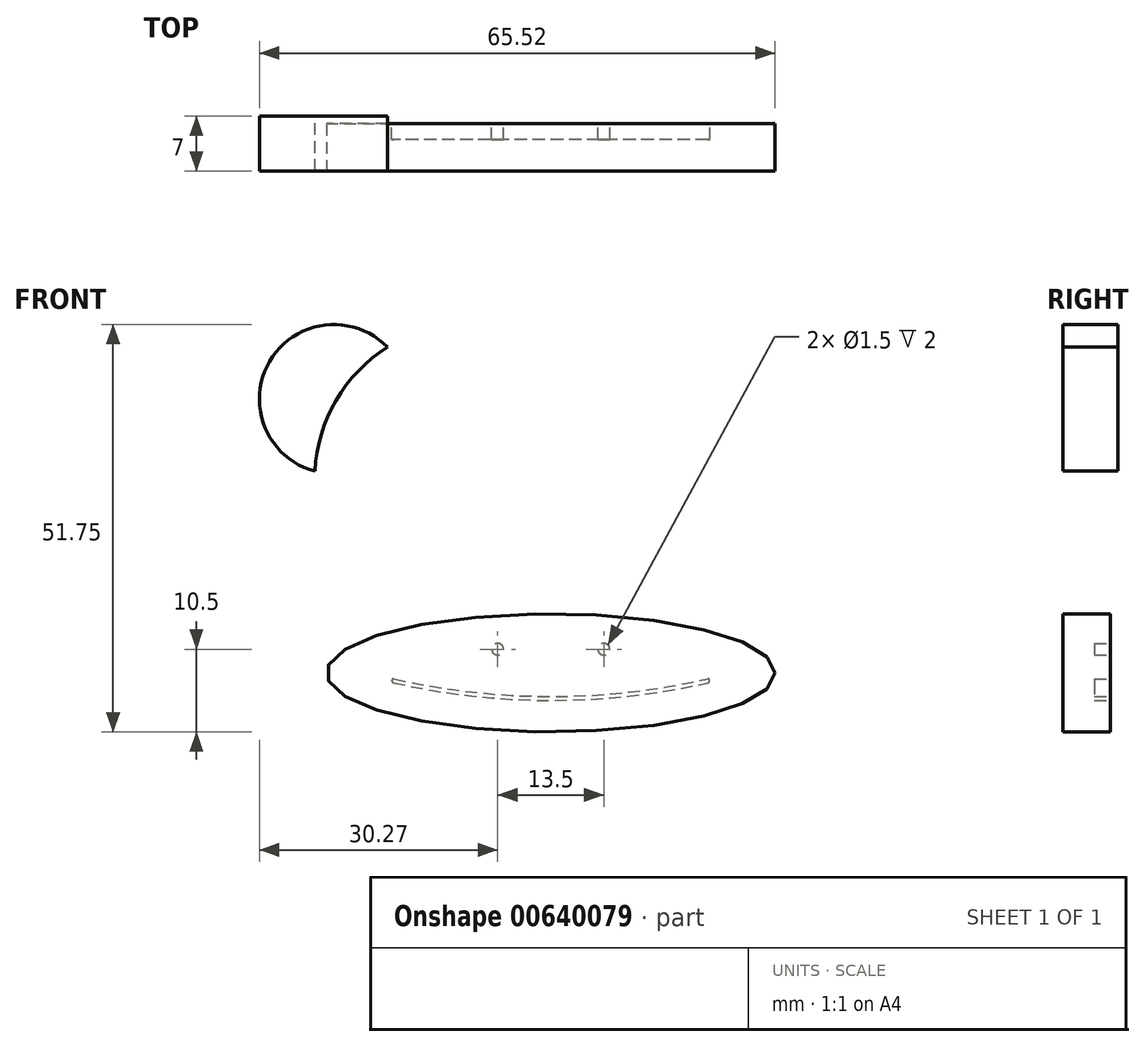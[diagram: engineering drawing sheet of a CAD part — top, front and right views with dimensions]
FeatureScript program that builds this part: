
annotation { "Feature Type Name" : "Feature", "Feature Type Description" : "" }
export const myFeature = defineFeature(function(context is Context, id is Id, definition is map)
    precondition{}
    {
        {
            var Q0;
            Q0=qCreatedBy(makeId("Front.planeOp"),FACE);
            var sketch = newSketch(context, id + "F0", { "sketchPlane" : qUnion([Q0])});
            skArc(sketch, "E0", {"start": v(28.27, -16.04) * mm, "mid": v(32, -5.67) * mm, "end": v(32.06, 5.36) * mm});
            skArc(sketch, "E1", {"start": v(32.06, 5.36) * mm, "mid": v(38.13, 23.57) * mm, "end": v(19.12, 26.28) * mm});
            skArc(sketch, "E2", {"start": v(-19.12, 26.28) * mm, "mid": v(-38.13, 23.57) * mm, "end": v(-32.06, 5.36) * mm});
            skEllipticalArc(sketch, "E3", {});
            skArc(sketch, "E4.trimOffspring", {"start": v(-32.06, 5.36) * mm, "mid": v(-32, -5.67) * mm, "end": v(-28.27, -16.04) * mm});
            skArc(sketch, "E5.trimOffspring", {"start": v(19.12, 26.28) * mm, "mid": v(0, 32.5) * mm, "end": v(-19.12, 26.28) * mm});
            const initialGuessF0  = {"E3": [0, -0.017, 1, 0, 0.0285, 0.0075, 3.0132996620008523, 0.12829299158894153]};
            skSetInitialGuess(sketch, initialGuessF0);
            skSolve(sketch);
        }
        {
            var Q0;
            {var subQ0=sQuery(id+"F0.wireOp",EDGE,"E2");Q0=makeQuery(id+"F0.imprint","IMPRINT",FACE,{"disambiguationData":[TD([[makeQuery(id+"F0.imprint","IMPRINT",EDGE,{"derivedFrom":subQ0}),1.0]])]});}
            var Q1;
            {var subQ0=sQuery(id+"F0.wireOp",EDGE,"E1");Q1=makeQuery(id+"F0.imprint","IMPRINT",FACE,{"disambiguationData":[TD([[makeQuery(id+"F0.imprint","IMPRINT",EDGE,{"derivedFrom":subQ0}),1.0]])]});}
            var Q2;
            {var subQ7=sQuery(id+"F0.wireOp",EDGE,"E3");Q2=makeQuery(id+"F0.imprint","IMPRINT",FACE,{"disambiguationData":[TD([[makeQuery(id+"F0.imprint","IMPRINT",EDGE,{"derivedFrom":subQ7}),1.0]])]});}
            extrude(context, id + "F1", {"entities" : qUnion([Q0, Q1, Q2]), "depth" : 7 * mm, "offsetDistance" : 25 * mm});
        }
        {
            var Q0;
            Q0=makeQuery(id+"F1.opExtrude","CAP_FACE",FACE,{"disambiguationData":[OSD([sQuery(id+"F0.wireOp",EDGE,"E0"),sQuery(id+"F0.wireOp",EDGE,"E1"),sQuery(id+"F0.wireOp",EDGE,"E2"),sQuery(id+"F0.wireOp",EDGE,"E3"),sQuery(id+"F0.wireOp",EDGE,"E4.trimOffspring"),sQuery(id+"F0.wireOp",EDGE,"E5.trimOffspring")])],"isStart":true});
            var sketch = newSketch(context, id + "F2", { "sketchPlane" : qUnion([Q0])});
            skEllipse(sketch, "E6", {"center": v(0, -17) * mm, "majorRadius": 28.5 * mm, "minorRadius": 7.5 * mm, "majorAxis": v(1, 0)});
            skFitSpline(sketch, "E7.0", {"points": [v(27.93, -17.56) * mm, v(28.03, -17) * mm, v(27.93, -16.44) * mm, v(27.6, -15.84) * mm, v(26.99, -15.2) * mm, v(26.1, -14.55) * mm, v(24.96, -13.91) * mm, v(23.57, -13.3) * mm, v(22.2, -12.81) * mm, v(21, -12.44) * mm, v(20.03, -12.18) * mm, v(19.02, -11.92) * mm, v(17.61, -11.6) * mm, v(15.75, -11.24) * mm, v(13.37, -10.87) * mm, v(10.87, -10.56) * mm, v(8.26, -10.31) * mm, v(5.57, -10.13) * mm, v(3.27, -10.04) * mm, v(1.4, -10) * mm, v(0, -10) * mm, v(-1.4, -10) * mm, v(-3.27, -10.04) * mm, v(-5.57, -10.13) * mm, v(-8.26, -10.31) * mm, v(-10.87, -10.56) * mm, v(-13.37, -10.87) * mm, v(-15.75, -11.24) * mm, v(-17.61, -11.6) * mm, v(-19.02, -11.92) * mm, v(-20.03, -12.18) * mm, v(-21, -12.44) * mm, v(-22.2, -12.81) * mm, v(-23.57, -13.3) * mm, v(-24.96, -13.91) * mm, v(-26.1, -14.55) * mm, v(-26.99, -15.2) * mm, v(-27.6, -15.84) * mm, v(-27.93, -16.44) * mm, v(-28.03, -17) * mm, v(-27.93, -17.56) * mm, v(-27.6, -18.16) * mm, v(-26.99, -18.8) * mm, v(-26.1, -19.45) * mm, v(-24.96, -20.09) * mm, v(-23.57, -20.7) * mm, v(-22.2, -21.19) * mm, v(-21, -21.56) * mm, v(-20.03, -21.82) * mm, v(-19.02, -22.08) * mm, v(-17.61, -22.4) * mm, v(-15.75, -22.76) * mm, v(-13.37, -23.13) * mm, v(-10.87, -23.44) * mm, v(-8.26, -23.69) * mm, v(-5.57, -23.87) * mm, v(-3.27, -23.96) * mm, v(-1.4, -24) * mm, v(0, -24) * mm, v(1.4, -24) * mm, v(3.27, -23.96) * mm, v(5.57, -23.87) * mm, v(8.26, -23.69) * mm, v(10.87, -23.44) * mm, v(13.37, -23.13) * mm, v(15.75, -22.76) * mm, v(17.61, -22.4) * mm, v(19.02, -22.08) * mm, v(20.03, -21.82) * mm, v(21, -21.56) * mm, v(22.2, -21.19) * mm, v(23.57, -20.7) * mm, v(24.96, -20.09) * mm, v(26.1, -19.45) * mm, v(26.99, -18.8) * mm, v(27.6, -18.16) * mm, v(27.93, -17.56) * mm, v(28.03, -17) * mm, v(27.93, -16.44) * mm, v(27.93, -17.56) * mm]});
            skSolve(sketch);
        }
        {
            var Q0;
            {var subQ0=sQuery(id+"F2.wireOp",EDGE,"E6");Q0=makeQuery(id+"F2.imprint","IMPRINT",FACE,{"disambiguationData":[TD([[makeQuery(id+"F2.imprint","IMPRINT",EDGE,{"disambiguationData":[OD(0.0)],"derivedFrom":subQ0}),1.0]])]});}
            var Q1;
            Q1 = qSketchRegion(id + "F4", true);
            extrude(context, id + "F3", {"entities" : qUnion([Q0, Q1]), "operationType" : NewBodyOperationType.REMOVE, "oppositeDirection" : true, "depth" : 1 * mm, "offsetDistance" : 25 * mm});
        }
        {
            var Q0;
            {var subQ0=sQuery(id+"F0.wireOp",EDGE,"E4.trimOffspring");var subQ1=sQuery(id+"F0.wireOp",EDGE,"E2");var subQ2=sQuery(id+"F0.wireOp",EDGE,"E1");var subQ3=sQuery(id+"F0.wireOp",EDGE,"E0");var subQ4=sQuery(id+"F0.wireOp",EDGE,"E5.trimOffspring");Q0=makeQuery(id+"F3.boolean.opBoolean","SPLIT",FACE,{"disambiguationData":[TD([makeQuery(id+"F1.opExtrude","SWEPT_FACE",FACE,{"disambiguationData":[OSD([subQ3])]})])],"derivedFrom":makeQuery(id+"F1.opExtrude","CAP_FACE",FACE,{"disambiguationData":[OSD([subQ3,subQ2,subQ1,sQuery(id+"F0.wireOp",EDGE,"E3"),subQ0,subQ4])],"isStart":true})});}
            var sketch = newSketch(context, id + "F4", { "sketchPlane" : qUnion([Q0])});
            skCircle(sketch, "E8", {"center": v(-9.5, 5) * mm, "radius": 1 * mm});
            skCircle(sketch, "E9", {"center": v(9.5, 5) * mm, "radius": 1 * mm});
            skArc(sketch, "E10", {"start": v(0, 12) * mm, "mid": v(-15.38, 17.78) * mm, "end": v(-26.83, 6) * mm});
            skArc(sketch, "E11", {"start": v(-26.83, 6) * mm, "mid": v(-25.12, -4.3) * mm, "end": v(-17.1, -11) * mm});
            skArc(sketch, "E12.MirrorCS", {"start": v(0, 12) * mm, "mid": v(15.38, 17.78) * mm, "end": v(26.83, 6) * mm});
            skArc(sketch, "E13.MirrorCS", {"start": v(26.83, 6) * mm, "mid": v(25.12, -4.3) * mm, "end": v(17.1, -11) * mm});
            skPoint(sketch, "E14", {"position": v(0, 0) * mm});
            skArc(sketch, "E15.0", {"start": v(-27.81, 6.2) * mm, "mid": v(-26, -4.8) * mm, "end": v(-17.43, -11.94) * mm});
            skArc(sketch, "E15.1", {"start": v(0, 13.6) * mm, "mid": v(-16.23, 18.6) * mm, "end": v(-27.81, 6.2) * mm});
            skArc(sketch, "E15.2", {"start": v(0, 13.6) * mm, "mid": v(16.23, 18.6) * mm, "end": v(27.81, 6.2) * mm});
            skArc(sketch, "E15.3", {"start": v(27.81, 6.2) * mm, "mid": v(26, -4.8) * mm, "end": v(17.43, -11.94) * mm});
            skSolve(sketch);
        }
        {
            var Q0;
            {var subQ0=sQuery(id+"F0.wireOp",EDGE,"E4.trimOffspring");var subQ1=sQuery(id+"F0.wireOp",EDGE,"E2");var subQ2=sQuery(id+"F0.wireOp",EDGE,"E1");var subQ3=sQuery(id+"F0.wireOp",EDGE,"E0");var subQ4=sQuery(id+"F0.wireOp",EDGE,"E5.trimOffspring");Q0=makeQuery(id+"F3.boolean.opBoolean","SPLIT",FACE,{"disambiguationData":[TD([makeQuery(id+"F1.opExtrude","SWEPT_FACE",FACE,{"disambiguationData":[OSD([subQ3])]})])],"derivedFrom":makeQuery(id+"F1.opExtrude","CAP_FACE",FACE,{"disambiguationData":[OSD([subQ3,subQ2,subQ1,sQuery(id+"F0.wireOp",EDGE,"E3"),subQ0,subQ4])],"isStart":true})});}
            var sketch = newSketch(context, id + "F5", { "sketchPlane" : qUnion([Q0])});
            skArc(sketch, "E16", {"start": v(-20.75, 24.37) * mm, "mid": v(-35.73, 22.55) * mm, "end": v(-29.95, 8.62) * mm});
            skArc(sketch, "E17", {"start": v(-20.75, 24.37) * mm, "mid": v(-27.27, 17.62) * mm, "end": v(-29.95, 8.62) * mm});
            skArc(sketch, "E18.MirrorCS", {"start": v(20.75, 24.37) * mm, "mid": v(27.27, 17.62) * mm, "end": v(29.95, 8.62) * mm});
            skArc(sketch, "E19.MirrorCS", {"start": v(20.75, 24.37) * mm, "mid": v(35.73, 22.55) * mm, "end": v(29.95, 8.62) * mm});
            skSolve(sketch);
        }
        {
            var Q0;
            Q0=makeQuery(id+"F4.imprint","IMPRINT",FACE,{"disambiguationData":[TD([[makeQuery(id+"F4.imprint","IMPRINT",EDGE,{"derivedFrom":sQuery(id+"F4.wireOp",EDGE,"E10")}),-1.0]])]});
            var Q1;
            Q1=makeQuery(id+"F4.imprint","IMPRINT",FACE,{"disambiguationData":[TD([[makeQuery(id+"F4.imprint","IMPRINT",EDGE,{"derivedFrom":sQuery(id+"F4.wireOp",EDGE,"E9")}),1.0]])]});
            var Q2;
            Q2=makeQuery(id+"F4.imprint","IMPRINT",FACE,{"disambiguationData":[TD([[makeQuery(id+"F4.imprint","IMPRINT",EDGE,{"derivedFrom":sQuery(id+"F4.wireOp",EDGE,"E8")}),1.0]])]});
            extrude(context, id + "F6", {"entities" : qUnion([Q0, Q1, Q2]), "operationType" : NewBodyOperationType.REMOVE, "oppositeDirection" : true, "depth" : 1 * mm, "offsetDistance" : 25 * mm});
        }
        {
            var Q0;
            Q0=makeQuery(id+"F5.imprint","IMPRINT",FACE,{"disambiguationData":[TD([[makeQuery(id+"F5.imprint","IMPRINT",EDGE,{"derivedFrom":sQuery(id+"F5.wireOp",EDGE,"E16")}),1.0]])]});
            var Q1;
            Q1=makeQuery(id+"F5.imprint","IMPRINT",FACE,{"disambiguationData":[TD([[makeQuery(id+"F5.imprint","IMPRINT",EDGE,{"derivedFrom":sQuery(id+"F5.wireOp",EDGE,"E18.MirrorCS")}),1.0]])]});
            extrude(context, id + "F7", {"entities" : qUnion([Q0, Q1]), "operationType" : NewBodyOperationType.REMOVE, "endBound" : BoundingType.THROUGH_ALL, "oppositeDirection" : true, "depth" : 25 * mm, "offsetDistance" : 25 * mm});
        }
        {
            var Q0;
            Q0=makeQuery(id+"F3.boolean.opBoolean","SPLIT",FACE,{"disambiguationData":[TD([makeQuery(id+"F3.opExtrude","SWEPT_FACE",FACE,{"disambiguationData":[OSD([sQuery(id+"F2.wireOp",EDGE,"E7.0")])]})])],"derivedFrom":makeQuery(id+"F1.opExtrude","CAP_FACE",FACE,{"disambiguationData":[OSD([sQuery(id+"F0.wireOp",EDGE,"E0"),sQuery(id+"F0.wireOp",EDGE,"E1"),sQuery(id+"F0.wireOp",EDGE,"E2"),sQuery(id+"F0.wireOp",EDGE,"E3"),sQuery(id+"F0.wireOp",EDGE,"E4.trimOffspring"),sQuery(id+"F0.wireOp",EDGE,"E5.trimOffspring")])],"isStart":true})});
            var sketch = newSketch(context, id + "F8", { "sketchPlane" : qUnion([Q0])});
            skCircle(sketch, "E20", {"center": v(6.75, -14) * mm, "radius": 0.75 * mm});
            skCircle(sketch, "E21", {"center": v(-6.75, -14) * mm, "radius": 0.75 * mm});
            skArc(sketch, "E22", {"start": v(-20, -18.25) * mm, "mid": v(0, -20.5) * mm, "end": v(20, -18.25) * mm});
            skArc(sketch, "E23.0", {"start": v(-19.89, -17.76) * mm, "mid": v(0, -20) * mm, "end": v(19.89, -17.76) * mm});
            skArc(sketch, "E24", {"start": v(-19.89, -17.76) * mm, "mid": v(-20.19, -17.95) * mm, "end": v(-20, -18.25) * mm});
            skArc(sketch, "E25", {"start": v(20, -18.25) * mm, "mid": v(20.19, -17.95) * mm, "end": v(19.89, -17.76) * mm});
            skSolve(sketch);
        }
        {
            var Q0;
            Q0 = qSketchRegion(id + "F8", true);
            extrude(context, id + "F9", {"entities" : qUnion([Q0]), "operationType" : NewBodyOperationType.REMOVE, "oppositeDirection" : true, "depth" : 3 * mm, "offsetDistance" : 25 * mm});
        }
    });
